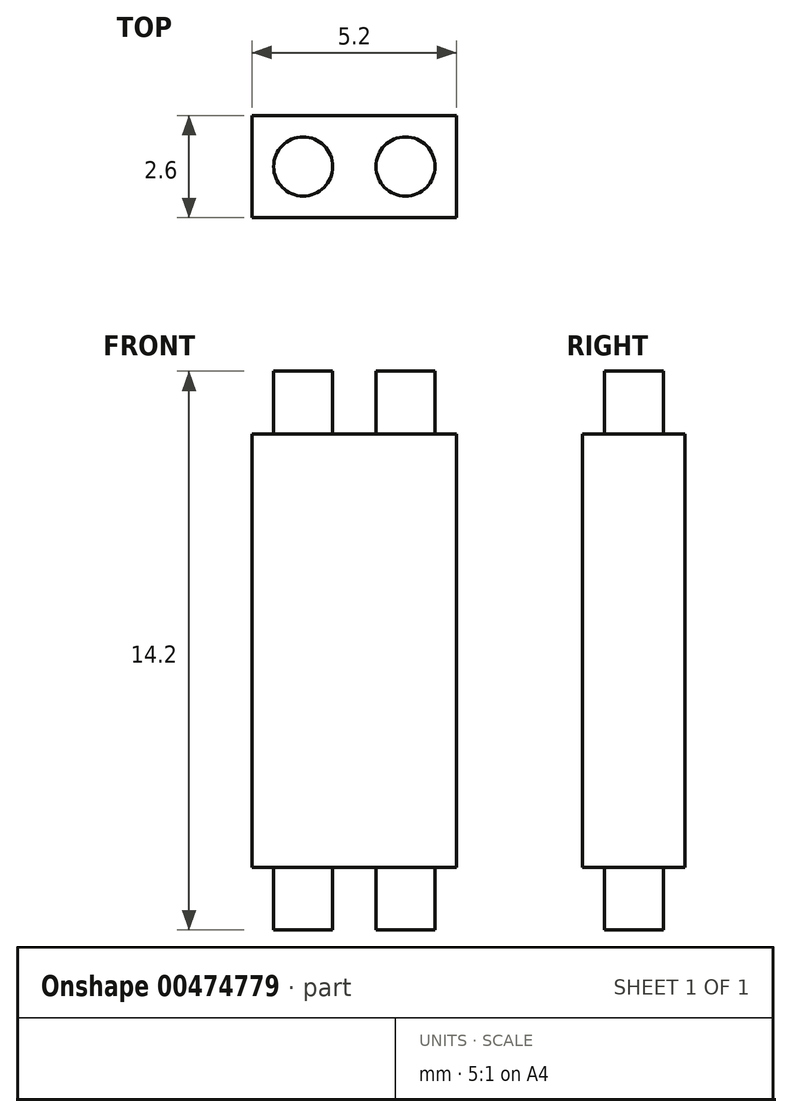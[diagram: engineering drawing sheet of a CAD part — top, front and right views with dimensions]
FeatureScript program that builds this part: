
annotation { "Feature Type Name" : "Feature", "Feature Type Description" : "" }
export const myFeature = defineFeature(function(context is Context, id is Id, definition is map)
    precondition{}
    {
        {
            var Q0;
            Q0=qCreatedBy(makeId("Top.planeOp"),FACE);
            var sketch = newSketch(context, id + "F0", { "sketchPlane" : qUnion([Q0])});
            skLineSegment(sketch, "E0.bottom", {"start": v(0, 0) * mm, "end": v(5.2, 0) * mm});
            skLineSegment(sketch, "E0.top", {"start": v(0, 2.6) * mm, "end": v(5.2, 2.6) * mm});
            skLineSegment(sketch, "E0.left", {"start": v(0, 0) * mm, "end": v(0, 2.6) * mm});
            skLineSegment(sketch, "E0.right", {"start": v(5.2, 0) * mm, "end": v(5.2, 2.6) * mm});
            skSolve(sketch);
        }
        {
            var Q0;
            Q0 = qSketchRegion(id + "F0", true);
            extrude(context, id + "F1", {"entities" : qUnion([Q0]), "depth" : 11 * mm});
        }
        {
            var Q0;
            Q0=makeQuery(id+"F1.opExtrude","CAP_FACE",FACE,{"disambiguationData":[OSD([sQuery(id+"F0.wireOp",EDGE,"E0.bottom"),sQuery(id+"F0.wireOp",EDGE,"E0.top"),sQuery(id+"F0.wireOp",EDGE,"E0.left"),sQuery(id+"F0.wireOp",EDGE,"E0.right")])],"isStart":false});
            var sketch = newSketch(context, id + "F2", { "sketchPlane" : qUnion([Q0])});
            skCircle(sketch, "E1", {"center": v(1.3, 1.3) * mm, "radius": 0.75 * mm});
            skCircle(sketch, "E2", {"center": v(3.9, 1.3) * mm, "radius": 0.75 * mm});
            skLineSegment(sketch, "E3", {"start": v(0, 1.3) * mm, "end": v(5.2, 1.3) * mm, "construction": true});
            skSolve(sketch);
        }
        {
            var Q0;
            Q0 = qSketchRegion(id + "F2", true);
            extrude(context, id + "F3", {"entities" : qUnion([Q0]), "operationType" : NewBodyOperationType.ADD, "depth" : 1.6 * mm});
        }
        {
            var Q0;
            Q0=makeQuery(id+"F1.opExtrude","CAP_FACE",FACE,{"disambiguationData":[OSD([sQuery(id+"F0.wireOp",EDGE,"E0.bottom"),sQuery(id+"F0.wireOp",EDGE,"E0.top"),sQuery(id+"F0.wireOp",EDGE,"E0.left"),sQuery(id+"F0.wireOp",EDGE,"E0.right")])],"isStart":true});
            var sketch = newSketch(context, id + "F4", { "sketchPlane" : qUnion([Q0])});
            skCircle(sketch, "E4", {"center": v(1.3, -1.3) * mm, "radius": 0.75 * mm});
            skCircle(sketch, "E5", {"center": v(3.9, -1.3) * mm, "radius": 0.75 * mm});
            skLineSegment(sketch, "E6", {"start": v(0, -1.3) * mm, "end": v(5.2, -1.3) * mm, "construction": true});
            skSolve(sketch);
        }
        {
            var Q0;
            Q0 = qSketchRegion(id + "F4", true);
            extrude(context, id + "F5", {"entities" : qUnion([Q0]), "operationType" : NewBodyOperationType.ADD, "depth" : 1.6 * mm});
        }
    });
